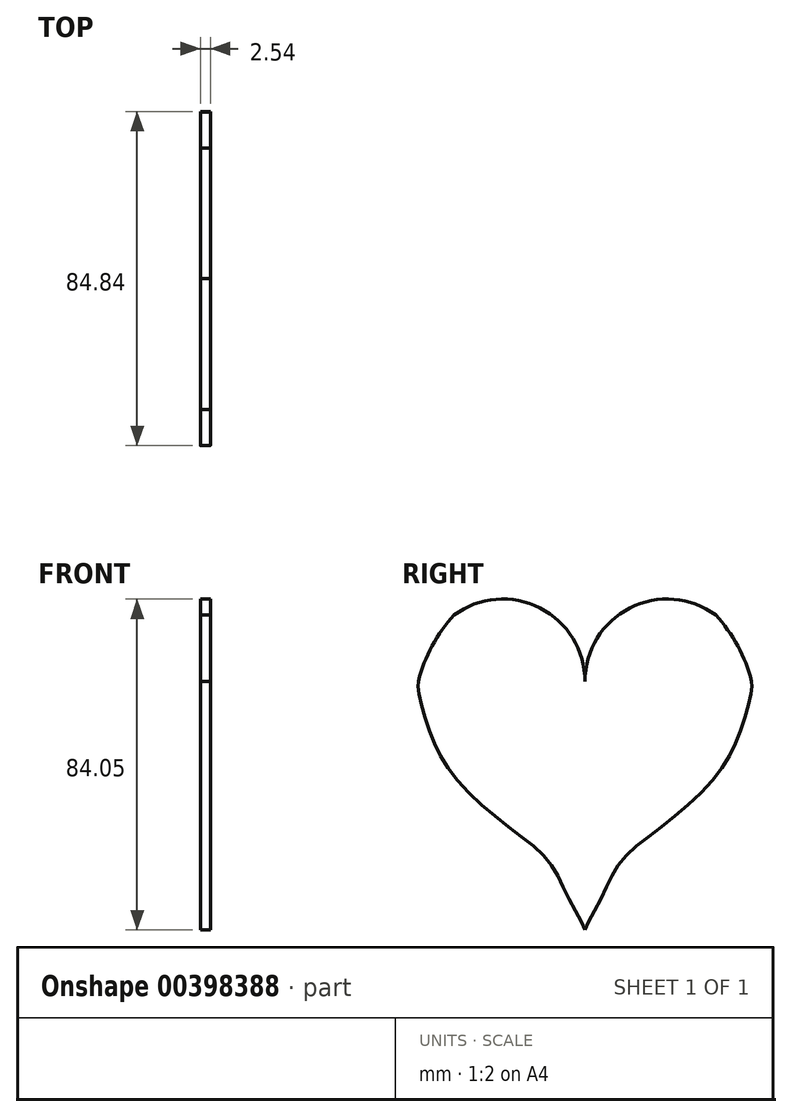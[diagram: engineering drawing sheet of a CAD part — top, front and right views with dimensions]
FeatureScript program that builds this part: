
annotation { "Feature Type Name" : "Feature", "Feature Type Description" : "" }
export const myFeature = defineFeature(function(context is Context, id is Id, definition is map)
    precondition{}
    {
        {
            var Q0;
            Q0=qCreatedBy(makeId("Right.planeOp"),FACE);
            var sketch = newSketch(context, id + "F0", { "sketchPlane" : qUnion([Q0])});
            skLineSegment(sketch, "E0", {"start": v(0, 0) * mm, "end": v(0, -48.66) * mm});
            skArc(sketch, "E1", {"start": v(33.22, 16.84) * mm, "mid": v(11.44, 18.62) * mm, "end": v(0, 0) * mm});
            skArc(sketch, "E2.MirrorCS", {"start": v(-33.22, 16.84) * mm, "mid": v(-11.44, 18.62) * mm, "end": v(0, 0) * mm});
            skArc(sketch, "E3", {"start": v(42.34, 0) * mm, "mid": v(38.82, 8.98) * mm, "end": v(33.22, 16.84) * mm});
            skArc(sketch, "E4.MirrorCS", {"start": v(-42.34, 0) * mm, "mid": v(-38.82, 8.98) * mm, "end": v(-33.22, 16.84) * mm});
            skFitSpline(sketch, "E5", {"points": [v(42.34, 0) * mm, v(42.34, -2.1) * mm, v(40, -11.23) * mm, v(34.16, -22.93) * mm, v(20.35, -36.26) * mm, v(9.12, -45.85) * mm, v(4.21, -54.98) * mm, v(0, -63.17) * mm, v(0, -63.87) * mm, v(0, -63.4) * mm], "startDerivative": vector(4, -28.8) * mm, "endDerivative": vector(-0.97, 23.74) * mm});
            skFitSpline(sketch, "E6.MirrorCS", {"points": [v(-42.34, 0) * mm, v(-42.34, -2.1) * mm, v(-40, -11.23) * mm, v(-34.16, -22.93) * mm, v(-20.35, -36.26) * mm, v(-9.12, -45.85) * mm, v(-4.21, -54.98) * mm, v(0, -63.17) * mm, v(0, -63.87) * mm, v(0, -63.4) * mm], "startDerivative": vector(-4, -28.8) * mm, "endDerivative": vector(0.97, 23.74) * mm});
            skSolve(sketch);
        }
        {
            var Q0;
            Q0=makeQuery(id+"F0.imprint","IMPRINT",FACE,{"disambiguationData":[TD([[makeQuery(id+"F0.imprint","IMPRINT",EDGE,{"derivedFrom":sQuery(id+"F0.wireOp",EDGE,"E1")}),1.0]])]});
            extrude(context, id + "F1", {"entities" : qUnion([Q0]), "depth" : 2.54 * mm});
        }
    });
